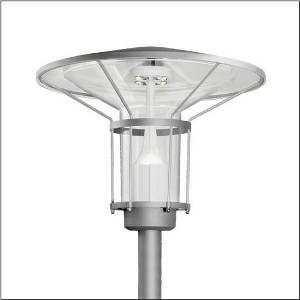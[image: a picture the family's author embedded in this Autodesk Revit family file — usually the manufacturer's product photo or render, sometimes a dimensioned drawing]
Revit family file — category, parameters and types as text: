
# Revit family: laterne_classic_iq___pl1_2s_5xa5245jf14h000022_9e24
name_source: partatom
category: Lighting Fixtures
units: mm (PartAtom-declared; Revit-internal decimal feet)

## family parameters
Cut with Voids When Loaded = No
Host = Face
Light Source = No
Part Type = Normal
Room Calculation Point = No
Round Connector Dimension = Use Diameter
Shared = No

## types (1)
- --- (1 x LED, 2660 lm, 19.3 W, 3000K)
    Apparent Load = 19 VA
    CIE Flux Codes = 21 60 93 97 100
    Color Rendering = 70
    Color Temperature = 3000K
    Default Elevation = 1800 mm
    Description = Lantern Classic iQ, mast luminaire, Module 540 iQ-SR, primary light control with 3 zone facetted reflector, of plastic, silver coated, highly specular, structured, primary optical cover: cover, of PMMA, transparent, light distribution: PL1.2s, light emission: direct distribution, primary light characteristic: symmetric, installation type: post-top, LED, High Power LED, rated luminous flux: 2.660lm, luminous efficacy: 138lm/W, light colour: 730, colour temperature: 3000K, control gear: iQ Street-Remote, control: Street-Remote, Auto-Match, Temp-Guard, Lumen-Switch, Night-Set, Smart-Wire, Light-Fading, Desk-Remote (wireless, voltage-free reading and setting of iQ features in the workshop via application-optimized NFC function/RFID function), optimised constant luminous flux control (CLO 2.0), pre-setting: logarithmic dimming characteristic, mains connection: 230..240V, AC, 50/60Hz, connection cable pre-assembled, cable length: 5,5m, wiring characteristics: H07RN-F, start of lifetime: 19W, end of service life: 21W, reduction: 10W, luminaire housing, upper part, of glass-fibre reinforced polyester, coated, Siteco® metallic grey (DB 702S), diameter: 750mm, height: 596mm, spigot size: d x l = 76 x 70mm (post-top) | with reducer (optional accessory) 60 x 70mm, mounting height: 3..5m, post-top mast mounting element, of diecast aluminium, coated, Siteco® metallic grey (DB 702S), Module 540 iQ-SR, traffic white (RAL 9016), equipment: standard, protection rating (complete): IP65, insulation class (complete): insulation class II (safety insulation), certification: CE, ENEC, VDE, packaging unit: 1 piece

Light Distribution: PL1.2s
    Height = 596 mm
    Lamp = 1 x LED
    Lamp Light Flux = 2660 lm
    Lamp Power = 19.3 W
    Lamp count = 1
    Length = 750 mm
    Luminous efficacy = 138 lm/W
    Manufacturer = Siteco
    ModVariant = No
    Model = 5XA5245JF14H000022
    Number of Poles = 1
    OnlyDefault = Yes
    Power Factor = 1
    Product Name = Laterne Classic iQ | PL1.2s
    Product group = mast luminaire | pylon top
    ProductGroupID = 6100
    Protection Class = Protection class II
    Protection Degree = IP 65
    RLX_Detail_Level = 1
    RLX_Emergency_Light_Flux = 0 lm
    RLX_Emergency_Type = 0
    RLX_Emergency_Type_DB = No
    RlxData = <blob elided: 37833 chars, md5=8d9a6281>
    Socket = socket
    Standby Power = 0 W
    System Light Flux = 2660 lm
    System Power = 19 W
    Type Comments = factory setting: luminous flux: 100 % | dim-lin: 254 | 403 mA
    Type Image = l_1006052.jpg
    URL = http://relux.com
    VarID = @adj_145668
    Voltage = 0 V
    Weight = 0.00 kg
    Width = 0 mm  [stored 0 ft]

note: [stored X ft] marks values corroborated as IEEE doubles in the binary element streams (Revit-internal decimal feet)

## geometry (parser evidence)
native form markers: Blend x4, Sweep x11
no freeform markers — native parametric forms only
